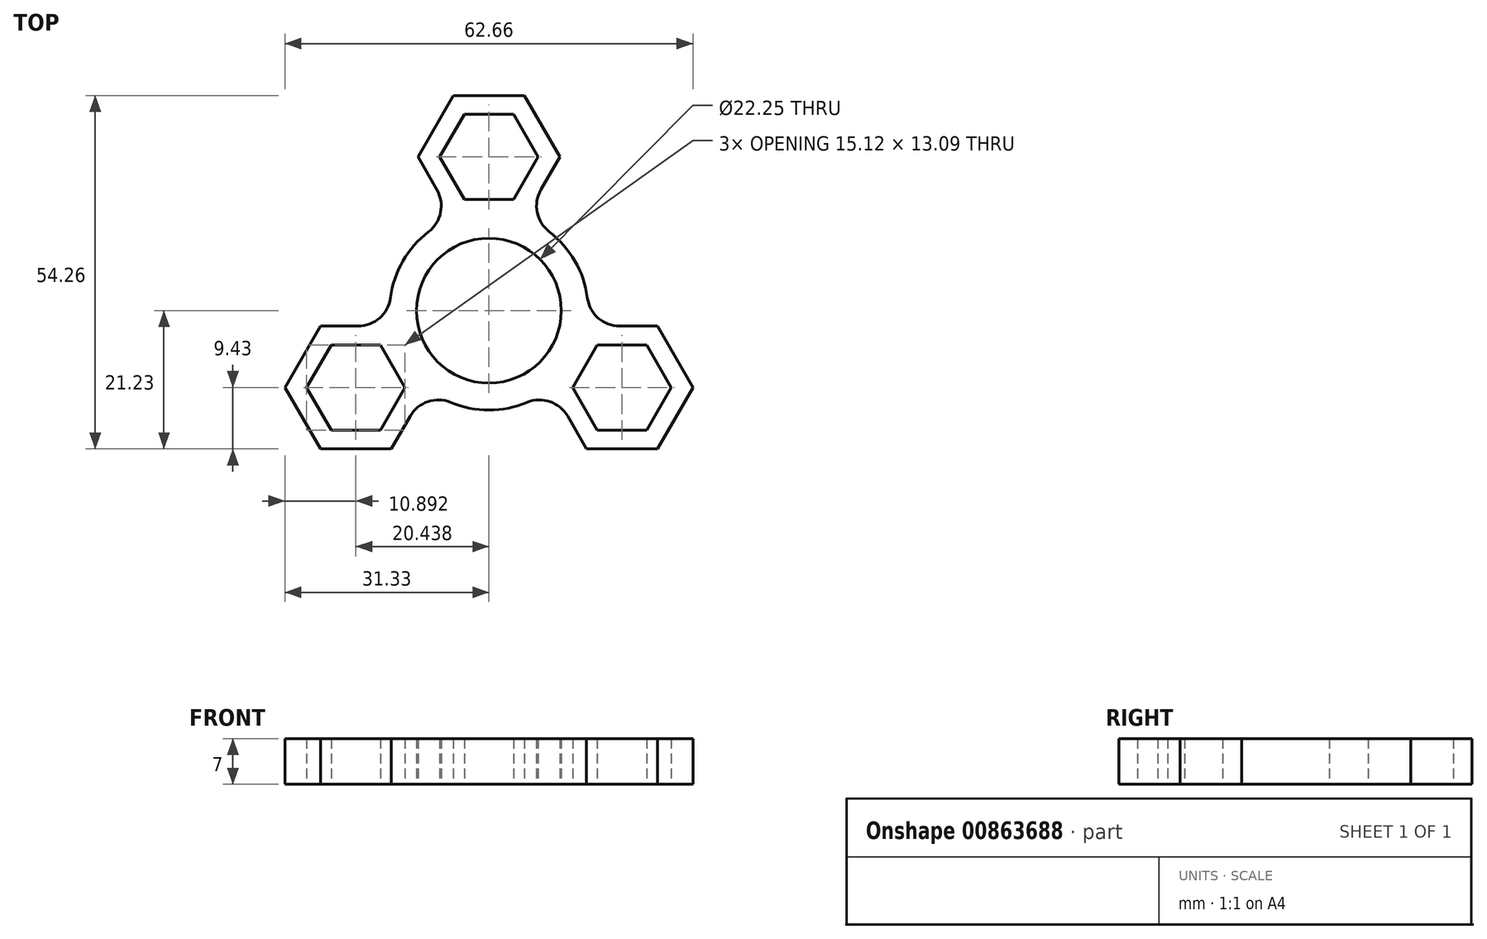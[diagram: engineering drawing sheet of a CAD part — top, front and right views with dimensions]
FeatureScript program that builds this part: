
annotation { "Feature Type Name" : "Feature", "Feature Type Description" : "" }
export const myFeature = defineFeature(function(context is Context, id is Id, definition is map)
    precondition{}
    {
        {
            var Q0;
            Q0=qCreatedBy(makeId("Top.planeOp"),FACE);
            var sketch = newSketch(context, id + "F0", { "sketchPlane" : qUnion([Q0])});
            skLineSegment(sketch, "E0", {"start": v(0, 23.6) * mm, "end": v(0, 33.03) * mm});
            skLineSegment(sketch, "E1.0", {"start": v(-5.44, 33.03) * mm, "end": v(5.44, 33.03) * mm});
            skLineSegment(sketch, "E1.1", {"start": v(5.44, 33.03) * mm, "end": v(10.89, 23.6) * mm});
            skLineSegment(sketch, "E1.2", {"start": v(10.89, 23.6) * mm, "end": v(5.44, 14.17) * mm});
            skLineSegment(sketch, "E1.4", {"start": v(-5.56, 14.37) * mm, "end": v(-10.89, 23.6) * mm});
            skLineSegment(sketch, "E1.5", {"start": v(-10.89, 23.6) * mm, "end": v(-5.44, 33.03) * mm});
            skPoint(sketch, "E1.0.midPoint", {"position": v(0, 33.03) * mm});
            skLineSegment(sketch, "E2.0", {"start": v(-3.78, 30.15) * mm, "end": v(3.78, 30.15) * mm});
            skLineSegment(sketch, "E2.1", {"start": v(3.78, 30.15) * mm, "end": v(7.56, 23.6) * mm});
            skLineSegment(sketch, "E2.2", {"start": v(7.56, 23.6) * mm, "end": v(3.78, 17.05) * mm});
            skLineSegment(sketch, "E2.3", {"start": v(3.78, 17.05) * mm, "end": v(-3.78, 17.05) * mm});
            skLineSegment(sketch, "E2.4", {"start": v(-3.78, 17.05) * mm, "end": v(-7.56, 23.6) * mm});
            skLineSegment(sketch, "E2.5", {"start": v(-7.56, 23.6) * mm, "end": v(-3.78, 30.15) * mm});
            skPoint(sketch, "E2.0.midPoint", {"position": v(0, 30.15) * mm});
            skPoint(sketch, "E3.1.2", {"position": v(-26.1, -15.07) * mm});
            skLineSegment(sketch, "E3.1.3", {"start": v(-31.33, -11.8) * mm, "end": v(-25.88, -2.37) * mm});
            skLineSegment(sketch, "E3.1.4", {"start": v(-25.88, -2.37) * mm, "end": v(-20.08, -2.37) * mm});
            skLineSegment(sketch, "E3.1.5", {"start": v(-12.88, -11.8) * mm, "end": v(-16.66, -18.35) * mm});
            skLineSegment(sketch, "E3.1.6", {"start": v(-16.66, -18.35) * mm, "end": v(-24.22, -18.35) * mm});
            skLineSegment(sketch, "E3.1.7", {"start": v(-15, -21.23) * mm, "end": v(-25.88, -21.23) * mm});
            skLineSegment(sketch, "E3.1.8", {"start": v(-16.66, -5.25) * mm, "end": v(-12.88, -11.8) * mm});
            skPoint(sketch, "E3.1.9", {"position": v(-28.6, -16.51) * mm});
            skLineSegment(sketch, "E3.1.10", {"start": v(-25.88, -21.23) * mm, "end": v(-31.33, -11.8) * mm});
            skLineSegment(sketch, "E3.1.11", {"start": v(-12.1, -16.2) * mm, "end": v(-15, -21.23) * mm});
            skLineSegment(sketch, "E3.1.12", {"start": v(-24.22, -5.25) * mm, "end": v(-16.66, -5.25) * mm});
            skLineSegment(sketch, "E3.1.13", {"start": v(-24.22, -18.35) * mm, "end": v(-28, -11.8) * mm});
            skLineSegment(sketch, "E3.1.14", {"start": v(-28, -11.8) * mm, "end": v(-24.22, -5.25) * mm});
            skPoint(sketch, "E3.2.2", {"position": v(26.1, -15.07) * mm});
            skLineSegment(sketch, "E3.2.3", {"start": v(25.88, -21.23) * mm, "end": v(15, -21.23) * mm});
            skLineSegment(sketch, "E3.2.4", {"start": v(15, -21.23) * mm, "end": v(9.55, -11.8) * mm});
            skLineSegment(sketch, "E3.2.5", {"start": v(16.66, -5.25) * mm, "end": v(24.22, -5.25) * mm});
            skLineSegment(sketch, "E3.2.6", {"start": v(24.22, -5.25) * mm, "end": v(28, -11.8) * mm});
            skLineSegment(sketch, "E3.2.7", {"start": v(25.88, -2.37) * mm, "end": v(31.33, -11.8) * mm});
            skLineSegment(sketch, "E3.2.8", {"start": v(12.88, -11.8) * mm, "end": v(16.66, -5.25) * mm});
            skPoint(sketch, "E3.2.9", {"position": v(28.6, -16.52) * mm});
            skLineSegment(sketch, "E3.2.10", {"start": v(31.33, -11.8) * mm, "end": v(25.88, -21.23) * mm});
            skLineSegment(sketch, "E3.2.11", {"start": v(20.08, -2.37) * mm, "end": v(25.88, -2.37) * mm});
            skLineSegment(sketch, "E3.2.12", {"start": v(16.66, -18.35) * mm, "end": v(12.88, -11.8) * mm});
            skLineSegment(sketch, "E3.2.13", {"start": v(28, -11.8) * mm, "end": v(24.22, -18.35) * mm});
            skLineSegment(sketch, "E3.2.14", {"start": v(24.22, -18.35) * mm, "end": v(16.66, -18.35) * mm});
            skPoint(sketch, "E3.center", {"position": v(0, 0) * mm});
            skArc(sketch, "E4", {"start": v(-9.28, 12.1) * mm, "mid": v(-13.2, 7.63) * mm, "end": v(-15.12, 1.98) * mm});
            skCircle(sketch, "E5", {"center": v(0, 0) * mm, "radius": 11.12 * mm});
            skLineSegment(sketch, "E6", {"start": v(-10.89, 23.6) * mm, "end": v(-7.99, 18.57) * mm});
            skLineSegment(sketch, "E7", {"start": v(10.89, 23.6) * mm, "end": v(7.99, 18.58) * mm});
            skLineSegment(sketch, "E8", {"start": v(25.88, -2.37) * mm, "end": v(13.97, -2.37) * mm});
            skLineSegment(sketch, "E9", {"start": v(15, -21.23) * mm, "end": v(12.1, -16.2) * mm});
            skLineSegment(sketch, "E10", {"start": v(-15, -21.23) * mm, "end": v(-8.98, -10.82) * mm});
            skLineSegment(sketch, "E11", {"start": v(-25.88, -2.37) * mm, "end": v(-13.5, -2.37) * mm});
            skArc(sketch, "E12.trimOffspring", {"start": v(-5.85, -14.09) * mm, "mid": v(0, -15.25) * mm, "end": v(5.85, -14.09) * mm});
            skArc(sketch, "E13.trimOffspring", {"start": v(15.12, 1.98) * mm, "mid": v(13.2, 7.63) * mm, "end": v(9.28, 12.1) * mm});
            skPoint(sketch, "E14.newPointB", {"position": v(-15, -2.37) * mm});
            skArc(sketch, "E14.filletArc", {"start": v(-20.08, -2.37) * mm, "mid": v(-16.78, -1.13) * mm, "end": v(-15.12, 1.98) * mm});
            skArc(sketch, "E15.filletArc", {"start": v(-9.28, 12.1) * mm, "mid": v(-7.42, 15.1) * mm, "end": v(-7.99, 18.57) * mm});
            skPoint(sketch, "E16.newPointA", {"position": v(15.22, -2.37) * mm});
            skArc(sketch, "E16.filletArc", {"start": v(15.12, 1.98) * mm, "mid": v(16.78, -1.13) * mm, "end": v(20.08, -2.37) * mm});
            skArc(sketch, "E17.filletArc", {"start": v(7.99, 18.58) * mm, "mid": v(7.41, 15.1) * mm, "end": v(9.28, 12.1) * mm});
            skPoint(sketch, "E18.newPointA", {"position": v(-9.66, -12) * mm});
            skArc(sketch, "E18.filletArc", {"start": v(-5.85, -14.09) * mm, "mid": v(-9.37, -13.97) * mm, "end": v(-12.1, -16.2) * mm});
            skArc(sketch, "E19.filletArc", {"start": v(12.1, -16.2) * mm, "mid": v(9.37, -13.97) * mm, "end": v(5.85, -14.09) * mm});
            skSolve(sketch);
        }
        {
            var Q0;
            Q0 = qSketchRegion(id + "F0", true);
            extrude(context, id + "F1", {"entities" : qUnion([Q0]), "depth" : 7 * mm, "offsetDistance" : 25 * mm});
        }
    });
